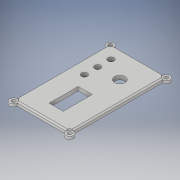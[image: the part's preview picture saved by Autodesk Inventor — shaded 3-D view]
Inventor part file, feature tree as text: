
AUTODESK INVENTOR PART (.ipt)
format: ipt  version: 2019 (Build 230136000, 136)  size: 219,136 bytes
history: native  units: mm
features: extrude x6, sketch x5, projected_geometry x3, chamfer x2
ambient origin geometry x8: Origin, YZ Plane, XZ Plane, XY Plane, X Axis, Y Axis, Z Axis, Center Point
bodies: Solid1 (feature_tree)
feature tree (16):
  extrude  "Extrusion1"  Depth=110.0mm
  extrude  "Extrusion2"  Depth=110.0mm
  extrude  "Extrusion3"  Depth=3.0mm
  extrude  "Extrusion4"  Depth=3.0mm TaperAngle=0.0deg
  sketch  "Sketch5"  dims[d24=16.0mm d25=33.0mm d26=24.0mm d27=24.0mm d28=16.5mm d29=3.0mm d30=0.0mm d31=6.8mm d32=6.8mm d33=6.8mm d34=15.125mm d35=15.125mm d36=15.125mm d37=15.125mm d38=6.0mm d39=0.0mm d40=20.0mm d42=110.0mm d43=20.0mm d45=64.0mm d48=1.5mm d49=0.0mm d50=1.5mm d51=2.0mm d52=45.0deg d53=16.0mm d54=55.0mm d55=12.0mm d56=23.0mm d58=1.5mm d59=0.0mm d60=1.5mm d61=2.0mm d62=45.0deg d64=30.0mm]
  extrude  "Extrusion6"  Depth=33.0mm
  chamfer  "Chamfer2"  Distance=24.0mm
  extrude  "Extrusion5"  Depth=24.0mm
  chamfer  "Chamfer1"  Distance=16.5mm
  sketch  "Sketch1"  dims[d0=64.0mm d1=110.0mm]
  sketch  "Sketch2"  dims[d2=8.485mm d3=20.0mm d5=110.0mm d6=20.0mm d8=64.0mm]
  projected_geometry  "Projected Loop1"
  sketch  "Sketch3"  dims[d11=3.0mm d12=0.0mm d13=4.3mm]
  sketch  "Sketch4"  dims[d14=20.0mm d16=110.0mm d17=20.0mm d19=64.0mm d22=3.0mm d23=0.0mm]
  projected_geometry  "Projected Loop2"
  projected_geometry  "Projected Loop3"
